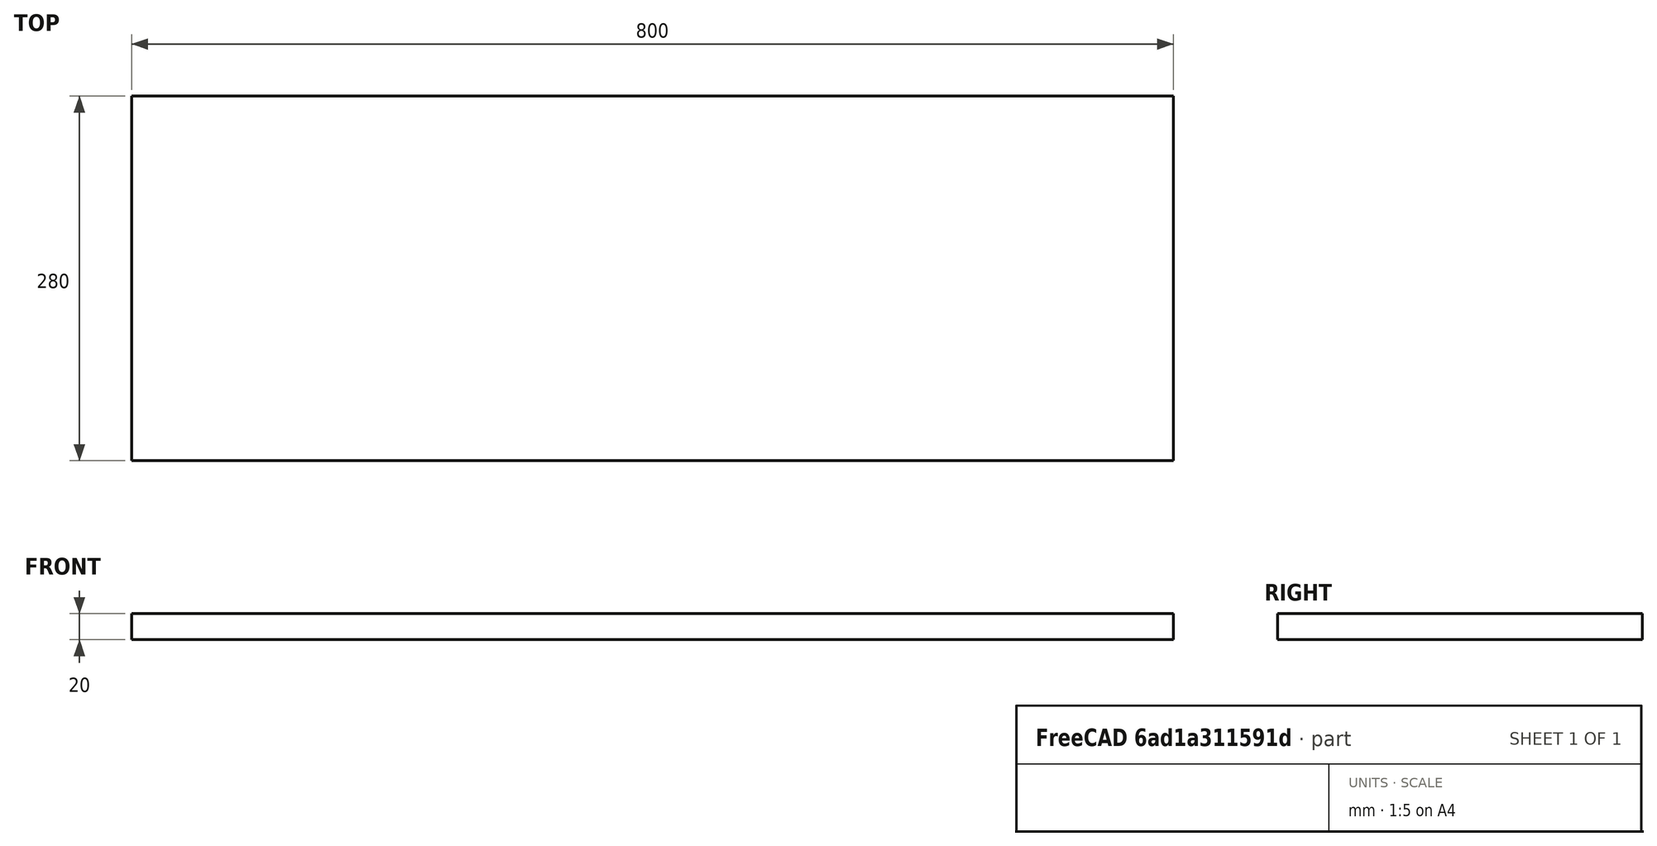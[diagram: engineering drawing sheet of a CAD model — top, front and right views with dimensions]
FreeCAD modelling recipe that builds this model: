
FCSTD DOCUMENT  (FreeCAD 0.20R29603 (Git))
Label: Schrägung
License: All rights reserved
LicenseURL: http://en.wikipedia.org/wiki/All_rights_reserved
objects: Sketcher::SketchObject×1, PartDesign::Pad×1, PartDesign::Body×1
note: 4 computed .brp shape members not serialized (recipe doc carries the construction recipe); baked Part::Feature solids carry a one-line shape summary decoded from their .brp

FEATURE [Sketcher::SketchObject] Sketch
  FullyConstrained = true
  MapMode = 5
  Support = -> [XY_Plane]
  sketch-geometry (5):
    g0: LineSegment StartX=-400 StartY=140 StartZ=0 EndX=-400 EndY=-140 EndZ=0
    g1: LineSegment StartX=-400 StartY=-140 StartZ=0 EndX=400 EndY=-140 EndZ=0
    g2: LineSegment StartX=400 StartY=-140 StartZ=0 EndX=400 EndY=140 EndZ=0
    g3: LineSegment StartX=400 StartY=140 StartZ=0 EndX=-400 EndY=140 EndZ=0
    g4: GeomPoint X=0 Y=0 Z=0
  constraints (12):
    c: Coincident(g0,g1)
    c: Coincident(g1,g2)
    c: Coincident(g2,g3)
    c: Coincident(g3,g0)
    c: Horizontal(g1)
    c: Horizontal(g3)
    c: Vertical(g0)
    c: Vertical(g2)
    c: Symmetric(g1,g0,g4)
    c: Coincident(g4,g-1)
    c: Distance(g2) = 280
    c: Distance(g3) = 800
FEATURE [PartDesign::Pad] Pad
  Direction = (0,0,1)
  Length = 20
  Length2 = 10
  Profile = -> Sketch
  ReferenceAxis = -> Sketch [N_Axis]
  Type = 0
FEATURE [PartDesign::Body] Body
  Group = -> [Sketch,Pad]
  Origin = -> Origin
  Tip = -> Pad
